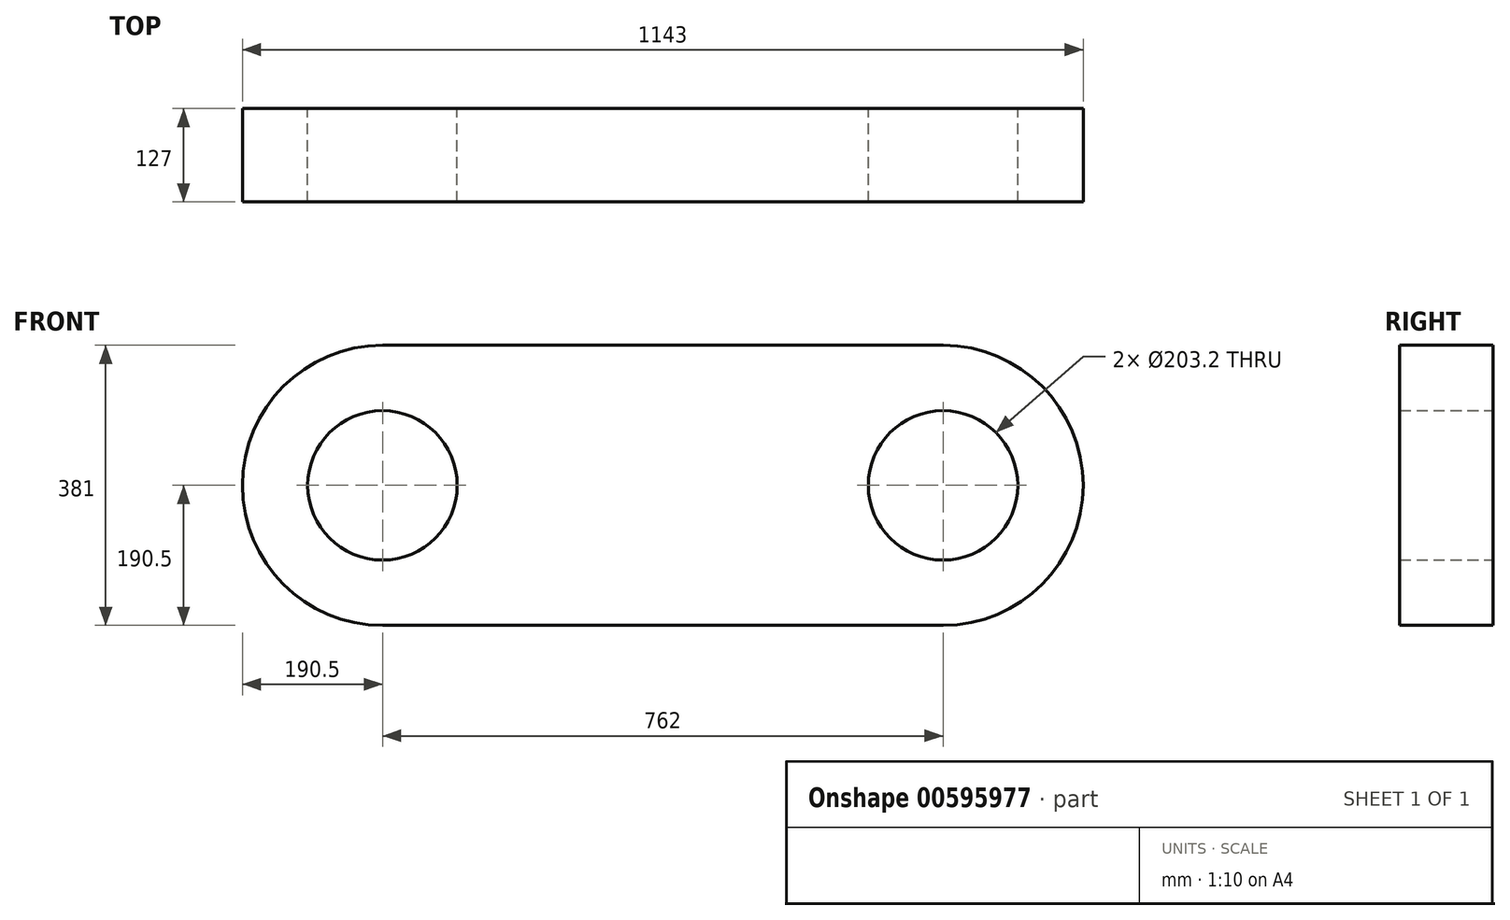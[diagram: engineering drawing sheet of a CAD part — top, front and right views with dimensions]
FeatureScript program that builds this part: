
annotation { "Feature Type Name" : "Feature", "Feature Type Description" : "" }
export const myFeature = defineFeature(function(context is Context, id is Id, definition is map)
    precondition{}
    {
        {
            var Q0;
            Q0=qCreatedBy(makeId("Front.planeOp"),FACE);
            var sketch = newSketch(context, id + "F0", { "sketchPlane" : qUnion([Q0])});
            skArc(sketch, "E0", {"start": v(0, 190.5) * mm, "mid": v(-190.5, 0) * mm, "end": v(0, -190.5) * mm});
            skArc(sketch, "E1", {"start": v(762, -190.5) * mm, "mid": v(952.5, 0) * mm, "end": v(762, 190.5) * mm});
            skLineSegment(sketch, "E2", {"start": v(0, 190.5) * mm, "end": v(762, 190.5) * mm});
            skLineSegment(sketch, "E3", {"start": v(0, -190.5) * mm, "end": v(762, -190.5) * mm});
            skCircle(sketch, "E4", {"center": v(0, 0) * mm, "radius": 101.6 * mm});
            skCircle(sketch, "E5", {"center": v(762, 0) * mm, "radius": 101.6 * mm});
            skSolve(sketch);
        }
        {
            var Q0;
            Q0=makeQuery(id+"F0.imprint","IMPRINT",FACE,{"disambiguationData":[TD([[makeQuery(id+"F0.imprint","IMPRINT",EDGE,{"derivedFrom":sQuery(id+"F0.wireOp",EDGE,"E0")}),1.0]])]});
            extrude(context, id + "F1", {"entities" : qUnion([Q0]), "depth" : 127 * mm, "offsetDistance" : 25.4 * mm});
        }
    });
